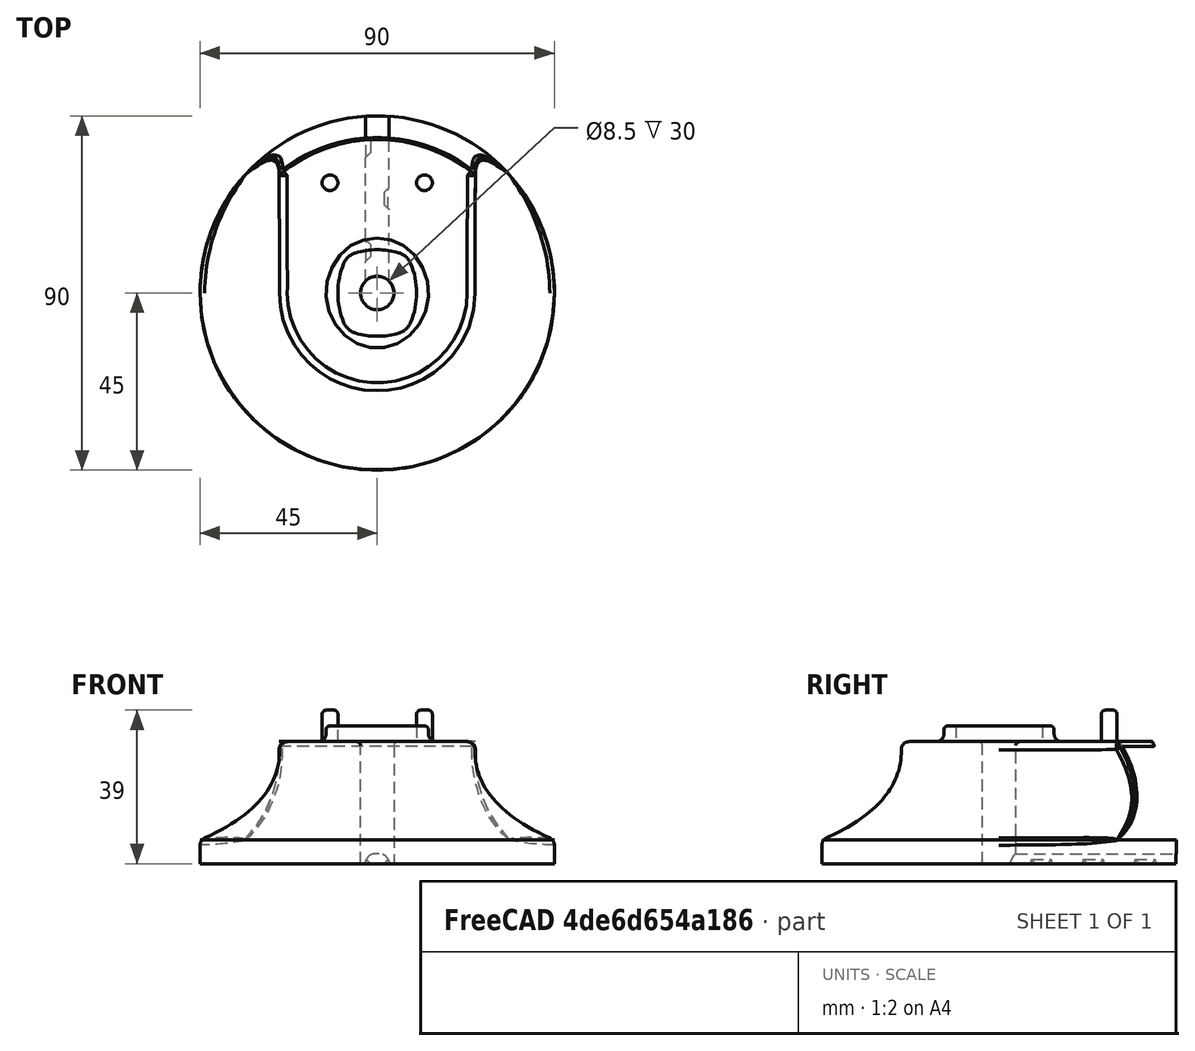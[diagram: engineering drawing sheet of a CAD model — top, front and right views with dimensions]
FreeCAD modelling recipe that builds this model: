
FCSTD DOCUMENT  (FreeCAD 1.0R39109 (Git))
Label: Toothbrush charging base
License: Creative Commons Attribution 4.0
LicenseURL: https://creativecommons.org/licenses/by/4.0/
objects: Sketcher::SketchObject×10, PartDesign::Pad×4, PartDesign::Pocket×3, PartDesign::Fillet×2, PartDesign::AdditiveLoft×1, PartDesign::Body×1
note: 51 computed .brp shape members not serialized (recipe doc carries the construction recipe); baked Part::Feature solids carry a one-line shape summary decoded from their .brp

FEATURE [Sketcher::SketchObject] Sketch
  ArcFitTolerance = 1e-06
  AttachmentSupport = -> [XY_Plane]
  FullyConstrained = true
  MakeInternals = false
  MapMode = 5
  sketch-geometry (1):
    g0: Circle CenterX=0 CenterY=0 CenterZ=0 NormalX=0 NormalY=0 NormalZ=1 AngleXU=0 Radius=45
  constraints (2):
    c: Diameter(g0) = 90
    c: Coincident(g0,g-1)
FEATURE [PartDesign::Pad] Pad
  Direction = (0,0,1)
  Length = 6
  Length2 = 10
  Profile = -> Sketch
  ReferenceAxis = -> Sketch [N_Axis]
  Suppressed = false
  Type = 0
FEATURE [Sketcher::SketchObject] Sketch001
  ArcFitTolerance = 1e-06
  AttachmentOffset = pos=(0,0,25) rot=(0,0,1;0rad)
  AttachmentSupport = -> [Pad]
  ExternalGeometry = -> [Pad]
  FullyConstrained = true
  MakeInternals = false
  MapMode = 5
  Placement = pos=(0,0,31) rot=(0,0,1;0rad)
  sketch-geometry (4):
    g0: ArcOfCircle CenterX=0 CenterY=0 CenterZ=0 NormalX=0 NormalY=0 NormalZ=1 AngleXU=0 Radius=39 StartAngle=0.874962 EndAngle=2.26663
    g1: ArcOfCircle CenterX=0 CenterY=0 CenterZ=0 NormalX=0 NormalY=0 NormalZ=1 AngleXU=0 Radius=25 StartAngle=3.14159 EndAngle=6.28319
    g2: LineSegment StartX=-25 StartY=29.9333 StartZ=0 EndX=-25 EndY=0 EndZ=0
    g3: LineSegment StartX=25 StartY=29.9333 StartZ=0 EndX=25 EndY=0 EndZ=0
  constraints (11):
    c: Coincident(g0,g-1)
    c: Coincident(g1,g0)
    c: PointOnObject(g1,g-1)
    c: PointOnObject(g1,g-1)
    c: DistanceX(g1,g1) = 50
    c: Vertical(g0,g1)
    c: Distance(g0,g-3) = 6
    c: Coincident(g2,g0)
    c: Coincident(g2,g1)
    c: Coincident(g3,g0)
    c: Tangent(g3,g1) = 1.5708
FEATURE [Sketcher::SketchObject] Sketch002
  ArcFitTolerance = 1e-06
  AttachmentOffset = pos=(0,0,20) rot=(0,0,1;0rad)
  AttachmentSupport = -> [Pad]
  ExternalGeometry = -> [Pad,Sketch001]
  FullyConstrained = true
  MakeInternals = false
  MapMode = 5
  Placement = pos=(0,0,26) rot=(0,0,1;0rad)
  sketch-geometry (4):
    g0: ArcOfCircle CenterX=0 CenterY=0 CenterZ=0 NormalX=0 NormalY=0 NormalZ=1 AngleXU=0 Radius=25 StartAngle=3.14159 EndAngle=6.28319
    g1: ArcOfCircle CenterX=0 CenterY=0 CenterZ=0 NormalX=0 NormalY=0 NormalZ=1 AngleXU=0 Radius=41 StartAngle=0.915044 EndAngle=2.22655
    g2: LineSegment StartX=-25 StartY=32.4962 StartZ=0 EndX=-25 EndY=0 EndZ=0
    g3: LineSegment StartX=25 StartY=32.4962 StartZ=0 EndX=25 EndY=0 EndZ=0
  constraints (11):
    c: Coincident(g0,g-1)
    c: Coincident(g0,g-4)
    c: Coincident(g1,g0)
    c: Vertical(g1,g0)
    c: Vertical(g1,g0)
    c: Coincident(g2,g1)
    c: Coincident(g2,g0)
    c: Coincident(g3,g1)
    c: Coincident(g3,g0)
    c: Horizontal(g0,g0)
    c: Distance(g1,g-3) = 4
FEATURE [Sketcher::SketchObject] Sketch003
  ArcFitTolerance = 1e-06
  AttachmentSupport = -> [Pad]
  ExternalGeometry = -> [Pad,Sketch001]
  FullyConstrained = true
  MakeInternals = false
  MapMode = 5
  Placement = pos=(0,0,6) rot=(0,0,1;0rad)
  sketch-geometry (4):
    g0: ArcOfCircle CenterX=0 CenterY=0 CenterZ=0 NormalX=0 NormalY=0 NormalZ=1 AngleXU=0 Radius=45 StartAngle=3.14159 EndAngle=6.28319
    g1: ArcOfCircle CenterX=0 CenterY=0 CenterZ=0 NormalX=0 NormalY=0 NormalZ=1 AngleXU=0 Radius=45 StartAngle=2.41385 EndAngle=3.14159
    g2: ArcOfCircle CenterX=-9e-16 CenterY=1.2e-15 CenterZ=0 NormalX=0 NormalY=0 NormalZ=1 AngleXU=0 Radius=45 StartAngle=0 EndAngle=0.72774
    g3: ArcOfCircle CenterX=-9e-16 CenterY=1.2e-15 CenterZ=0 NormalX=0 NormalY=0 NormalZ=1 AngleXU=0 Radius=45 StartAngle=0.72774 EndAngle=2.41385
  constraints (13):
    c: Coincident(g0,g-1)
    c: Horizontal(g0,g0)
    c: PointOnObject(g0,g-1)
    c: Coincident(g1,g0)
    c: Coincident(g1,g0)
    c: PointOnObject(g1,g-3)
    c: Horizontal(g1,g2)
    c: Coincident(g3,g2)
    c: Coincident(g3,g1)
    c: Coincident(g3,g2)
    c: Horizontal(g1,g-4)
    c: Coincident(g2,g0)
    c: PointOnObject(g2,g-3)
FEATURE [PartDesign::AdditiveLoft] AdditiveLoft
  BaseFeature = -> Pad
  Closed = false
  Profile = -> Sketch003
  Ruled = false
  Sections = -> [Sketch002,Sketch001]
  Suppressed = false
FEATURE [Sketcher::SketchObject] Sketch004
  ArcFitTolerance = 1e-06
  AttachmentSupport = -> [AdditiveLoft]
  FullyConstrained = true
  MakeInternals = false
  MapMode = 5
  Placement = pos=(0,0,31) rot=(0,0,1;0rad)
  sketch-geometry (18):
    g0: LineSegment [constr] StartX=-10 StartY=-11 StartZ=0 EndX=10 EndY=-11 EndZ=0
    g1: LineSegment [constr] StartX=10 StartY=-11 StartZ=0 EndX=10 EndY=11 EndZ=0
    g2: LineSegment [constr] StartX=10 StartY=11 StartZ=0 EndX=-10 EndY=11 EndZ=0
    g3: LineSegment [constr] StartX=-10 StartY=11 StartZ=0 EndX=-10 EndY=-11 EndZ=0
    g4: GeomPoint [constr] X=0 Y=0 Z=0
    g5: ArcOfCircle CenterX=0 CenterY=-8.28259 CenterZ=0 NormalX=0 NormalY=0 NormalZ=1 AngleXU=0 Radius=19.2826 StartAngle=1.28155 EndAngle=1.86004
    g6: ArcOfCircle CenterX=0 CenterY=8.28259 CenterZ=0 NormalX=0 NormalY=0 NormalZ=1 AngleXU=0 Radius=19.2826 StartAngle=4.42314 EndAngle=5.00164
    g7: ArcOfCircle CenterX=-9.5 CenterY=0 CenterZ=0 NormalX=0 NormalY=0 NormalZ=1 AngleXU=0 Radius=19.5 StartAngle=5.88839 EndAngle=6.67798
    g8: ArcOfCircle CenterX=9.5 CenterY=0 CenterZ=0 NormalX=0 NormalY=0 NormalZ=1 AngleXU=0 Radius=19.5 StartAngle=2.7468 EndAngle=3.53638
    g9: ArcOfCircle CenterX=-4.15846 CenterY=5.69103 CenterZ=0 NormalX=0 NormalY=0 NormalZ=1 AngleXU=0 Radius=4.70333 StartAngle=1.86004 EndAngle=2.7468
    g10: ArcOfCircle CenterX=4.15846 CenterY=5.69103 CenterZ=0 NormalX=0 NormalY=0 NormalZ=1 AngleXU=0 Radius=4.70333 StartAngle=0.394791 EndAngle=1.28155
    g11: ArcOfCircle CenterX=4.15846 CenterY=-5.69103 CenterZ=0 NormalX=0 NormalY=0 NormalZ=1 AngleXU=0 Radius=4.70333 StartAngle=5.00164 EndAngle=5.88839
    g12: ArcOfCircle CenterX=-4.15846 CenterY=-5.69103 CenterZ=0 NormalX=0 NormalY=0 NormalZ=1 AngleXU=0 Radius=4.70333 StartAngle=3.53638 EndAngle=4.42314
    g13: Ellipse CenterX=0 CenterY=0 CenterZ=0 NormalX=0 NormalY=0 NormalZ=1 MajorRadius=14 MinorRadius=13 AngleXU=1.5708
    g14: LineSegment [constr] StartX=0 StartY=14 StartZ=0 EndX=0 EndY=-14 EndZ=0
    g15: LineSegment [constr] StartX=-13 StartY=0 StartZ=0 EndX=13 EndY=0 EndZ=0
    g16: GeomPoint [constr] X=0 Y=5.19615 Z=0
    g17: GeomPoint [constr] X=0 Y=-5.19615 Z=0
  constraints (38):
    c: Coincident(g0,g1)
    c: Coincident(g1,g2)
    c: Coincident(g2,g3)
    c: Coincident(g3,g0)
    c: Horizontal(g0)
    c: Horizontal(g2)
    c: Vertical(g1)
    c: Vertical(g3)
    c: Symmetric(g2,g0,g4)
    c: Distance(g1,g3) = 20
    c: Distance(g0,g2) = 22
    c: Coincident(g4,g-1)
    c: PointOnObject(g5,g-2)
    c: Horizontal(g5,g5)
    c: Tangent(g5,g2)
    c: Symmetric(g6,g5,g4)
    c: Symmetric(g6,g5,g4)
    c: Horizontal(g6,g6)
    c: PointOnObject(g7,g-1)
    c: Tangent(g7,g1)
    c: Symmetric(g7,g8,g4)
    c: DistanceX(g5,g5) = 11
    c: DistanceY(g7,g7) = 15
    c: Tangent(g9,g5) = -1.5708
    c: Tangent(g9,g8) = -1.5708
    c: Tangent(g10,g5) = -1.5708
    c: Tangent(g10,g7) = -1.5708
    c: Tangent(g11,g7) = -1.5708
    c: Tangent(g11,g6) = -1.5708
    c: Tangent(g12,g6) = -1.5708
    c: Tangent(g12,g8) = -1.5708
    c: Equal(g9,g10)
    c: InternalAlignment(g14-g17 -> g13) x4
    c: Distance(g13,g15) = 13
    c: Angle(g15) = 0
    c: Distance(g13,g14) = 14
    c: Coincident(g13,g4)
    c: DistanceX(g7,g8) = 19
FEATURE [PartDesign::Pad] Pad001
  BaseFeature = -> AdditiveLoft
  Direction = (0,0,1)
  Length = 4
  Length2 = 10
  Profile = -> Sketch004
  ReferenceAxis = -> Sketch004 [N_Axis]
  Suppressed = false
  Type = 0
FEATURE [Sketcher::SketchObject] Sketch005
  ArcFitTolerance = 1e-06
  AttachmentSupport = -> [Pad001]
  FullyConstrained = true
  MakeInternals = false
  MapMode = 5
  Placement = pos=(0,0,31) rot=(0,0,1;0rad)
  sketch-geometry (2):
    g0: Circle CenterX=-12 CenterY=28 CenterZ=0 NormalX=0 NormalY=0 NormalZ=1 AngleXU=0 Radius=2
    g1: Circle CenterX=12 CenterY=28 CenterZ=0 NormalX=0 NormalY=0 NormalZ=1 AngleXU=0 Radius=2
  constraints (5):
    c: Diameter(g0) = 4
    c: Equal(g0,g1)
    c: Symmetric(g0,g1,g-2)
    c: DistanceY(g-1,g1) = 28
    c: DistanceX(g0,g1) = 24
FEATURE [PartDesign::Pad] Pad002
  BaseFeature = -> Pad001
  Direction = (0,0,1)
  Length = 8
  Length2 = 10
  Profile = -> Sketch005
  ReferenceAxis = -> Sketch005 [N_Axis]
  Suppressed = false
  Type = 0
FEATURE [Sketcher::SketchObject] Sketch006
  ArcFitTolerance = 1e-06
  AttachmentSupport = -> [Pad002]
  FullyConstrained = true
  MakeInternals = false
  MapMode = 5
  Placement = pos=(0,0,31) rot=(0,0,1;0rad)
  sketch-geometry (1):
    g0: Circle CenterX=0 CenterY=0 CenterZ=0 NormalX=0 NormalY=0 NormalZ=1 AngleXU=0 Radius=4.25
  constraints (2):
    c: Diameter(g0) = 8.5
    c: Coincident(g0,g-1)
FEATURE [PartDesign::Pocket] Pocket
  BaseFeature = -> Pad002
  Direction = (0,0,-1)
  Length = 5
  Length2 = 5
  Profile = -> Sketch006
  ReferenceAxis = -> Sketch006 [N_Axis]
  Suppressed = false
  Type = 1
FEATURE [Sketcher::SketchObject] Sketch007
  ArcFitTolerance = 1e-06
  AttachmentSupport = -> [XZ_Plane]
  FullyConstrained = true
  MakeInternals = false
  MapMode = 5
  Placement = pos=(0,0,0) rot=(1,0,0;1.5708rad)
  sketch-geometry (4):
    g0: ArcOfCircle CenterX=-0.5 CenterY=0 CenterZ=0 NormalX=0 NormalY=0 NormalZ=1 AngleXU=0 Radius=2.5 StartAngle=1.5708 EndAngle=3.14159
    g1: ArcOfCircle CenterX=0.5 CenterY=0 CenterZ=0 NormalX=0 NormalY=0 NormalZ=1 AngleXU=0 Radius=2.5 StartAngle=0 EndAngle=1.5708
    g2: LineSegment StartX=-0.5 StartY=2.5 StartZ=0 EndX=0.5 EndY=2.5 EndZ=0
    g3: LineSegment StartX=-3 StartY=0 StartZ=0 EndX=3 EndY=0 EndZ=0
  constraints (13):
    c: PointOnObject(g0,g-1)
    c: Vertical(g0,g0)
    c: Radius(g0) = 2.5
    c: Vertical(g1,g1)
    c: Horizontal(g0,g1)
    c: Coincident(g2,g0)
    c: Coincident(g2,g1)
    c: DistanceX(g0,g1) = 6
    c: PointOnObject(g0,g-1)
    c: PointOnObject(g1,g-1)
    c: Symmetric(g0,g1,g-1)
    c: Coincident(g3,g0)
    c: Coincident(g3,g1)
FEATURE [PartDesign::Pocket] Pocket001
  BaseFeature = -> Pocket
  Direction = (0,1,-2e-16)
  Length = 5
  Length2 = 5
  Profile = -> Sketch007
  ReferenceAxis = -> Sketch007 [N_Axis]
  Suppressed = false
  Type = 1
FEATURE [Sketcher::SketchObject] Sketch008
  ArcFitTolerance = 1e-06
  AttachmentSupport = -> [Pocket001]
  ExternalGeometry = -> [Pocket001]
  FullyConstrained = true
  MakeInternals = false
  MapMode = 5
  Placement = pos=(0,0,0) rot=(1,0,0;3.14159rad)
  sketch-geometry (16):
    g0: LineSegment StartX=-3 StartY=-39.8999 StartZ=0 EndX=-1.75 EndY=-38.6499 EndZ=0
    g1: LineSegment StartX=-1.75 StartY=-38.6499 StartZ=0 EndX=-1.75 EndY=-35.6499 EndZ=0
    g2: LineSegment StartX=-1.75 StartY=-35.6499 StartZ=0 EndX=-3 EndY=-34.3999 EndZ=0
    g3: LineSegment StartX=3 StartY=-26.7051 StartZ=0 EndX=1.75 EndY=-25.4551 EndZ=0
    g4: LineSegment StartX=1.75 StartY=-25.4551 StartZ=0 EndX=1.75 EndY=-22.4551 EndZ=0
    g5: LineSegment StartX=1.75 StartY=-22.4551 StartZ=0 EndX=3 EndY=-21.2051 EndZ=0
    g6: LineSegment StartX=3 StartY=-21.2051 StartZ=0 EndX=3 EndY=-26.7051 EndZ=0
    g7: LineSegment StartX=-3 StartY=-34.3999 StartZ=0 EndX=-3 EndY=-39.8999 EndZ=0
    g8: LineSegment StartX=-3 StartY=-13.5104 StartZ=0 EndX=-1.75 EndY=-12.2604 EndZ=0
    g9: LineSegment StartX=-1.75 StartY=-12.2604 StartZ=0 EndX=-1.75 EndY=-9.2604 EndZ=0
    g10: LineSegment StartX=-1.75 StartY=-9.2604 StartZ=0 EndX=-3 EndY=-8.0104 EndZ=0
    g11: LineSegment StartX=-3 StartY=-8.0104 StartZ=0 EndX=-3 EndY=-13.5104 EndZ=0
    g12: GeomPoint [constr] X=-3 Y=-10.7604 Z=0
    g13: GeomPoint [constr] X=3 Y=-23.9551 Z=0
    g14: GeomPoint [constr] X=-3 Y=-37.1499 Z=0
    g15: GeomPoint [constr] X=-3 Y=-23.9551 Z=0
  constraints (39):
    c: PointOnObject(g0,g-3)
    c: Coincident(g1,g0)
    c: Vertical(g1)
    c: Coincident(g2,g1)
    c: PointOnObject(g2,g-3)
    c: Angle(g-3,g0) = 2.35619
    c: Angle(g2,g-3) = 2.35619
    c: DistanceX(g0,g0) = 1.25
    c: DistanceY(g0,g1) = 3
    c: DistanceY(g-3,g0) = 5
    c: Coincident(g3,g4)
    c: Vertical(g4)
    c: Coincident(g4,g5)
    c: PointOnObject(g5,g-4)
    c: Coincident(g5,g6)
    c: Coincident(g6,g3)
    c: Coincident(g2,g7)
    c: Coincident(g7,g0)
    c: PointOnObject(g8,g-3)
    c: Coincident(g8,g9)
    c: Vertical(g9)
    c: Coincident(g9,g10)
    c: Coincident(g10,g11)
    c: Coincident(g11,g8)
    c: Equal(g1,g4)
    c: Angle(g5,g6) = 0.785398
    c: Angle(g6,g3) = 0.785398
    c: DistanceX(g3,g3) = 1.25
    c: Angle(g11,g10) = 0.785398
    c: Angle(g8,g11) = 0.785398
    c: Equal(g9,g4)
    c: Vertical(g1,g8)
    c: PointOnObject(g3,g-4)
    c: Symmetric(g11,g11,g12)
    c: Symmetric(g6,g6,g13)
    c: Symmetric(g7,g7,g14)
    c: Symmetric(g-3,g-3,g15)
    c: Symmetric(g12,g14,g15)
    c: Horizontal(g15,g13)
FEATURE [PartDesign::Pad] Pad003
  BaseFeature = -> Pocket001
  Direction = (0,0,-1)
  Length = 10
  Length2 = 10
  Profile = -> Sketch008
  ReferenceAxis = -> Sketch008 [N_Axis]
  Reversed = true
  Suppressed = false
  Type = 3
  UpToFace = -> Pocket001 [Face8]
FEATURE [Sketcher::SketchObject] Sketch009
  ArcFitTolerance = 1e-06
  AttachmentSupport = -> [XZ_Plane]
  ExternalGeometry = -> [Pad003]
  FullyConstrained = true
  MakeInternals = false
  MapMode = 5
  Placement = pos=(0,0,0) rot=(1,0,0;1.5708rad)
  sketch-geometry (6):
    g0: LineSegment StartX=1.75 StartY=5.7e-15 StartZ=0 EndX=2.77859 EndY=1.02859 EndZ=0
    g1: LineSegment StartX=-1.75 StartY=8.6e-15 StartZ=0 EndX=-2.77859 EndY=1.02859 EndZ=0
    g2: LineSegment StartX=0.5 StartY=2.5 StartZ=0 EndX=-0.5 EndY=2.5 EndZ=0
    g3: ArcOfCircle CenterX=0.5 CenterY=0 CenterZ=0 NormalX=0 NormalY=0 NormalZ=1 AngleXU=0 Radius=2.5 StartAngle=0.424031 EndAngle=1.5708
    g4: ArcOfCircle CenterX=-0.5 CenterY=0 CenterZ=0 NormalX=0 NormalY=0 NormalZ=1 AngleXU=0 Radius=2.5 StartAngle=1.5708 EndAngle=2.71756
    g5: LineSegment StartX=1.75 StartY=5.7e-15 StartZ=0 EndX=-1.75 EndY=8.6e-15 EndZ=0
  constraints (16):
    c: Coincident(g0,g-3)
    c: PointOnObject(g0,g-6)
    c: Angle(g-3,g0) = 0.785398
    c: Coincident(g1,g-4)
    c: PointOnObject(g1,g-5)
    c: Angle(g1,g-4) = 0.785398
    c: Coincident(g2,g-6)
    c: Coincident(g2,g-5)
    c: PointOnObject(g4,g-1)
    c: Coincident(g4,g1)
    c: Coincident(g4,g2)
    c: Coincident(g3,g0)
    c: Coincident(g3,g2)
    c: PointOnObject(g3,g-1)
    c: Coincident(g5,g0)
    c: Coincident(g5,g1)
FEATURE [PartDesign::Pocket] Pocket002
  BaseFeature = -> Pad003
  Direction = (0,1,-2e-16)
  Length = 5
  Length2 = 5
  Profile = -> Sketch009
  ReferenceAxis = -> Sketch009 [N_Axis]
  Refine = true
  Suppressed = false
  Type = 1
FEATURE [PartDesign::Fillet] Fillet
  Base = -> Pocket002 [Edge28,Edge15,Edge18,Edge20,Edge19,Edge10]
  BaseFeature = -> Pocket002
  Radius = 2
  SupportTransform = false
  Suppressed = false
  UseAllEdges = false
FEATURE [PartDesign::Fillet] Fillet001
  Base = -> Fillet [Edge120,Edge118,Edge121,Edge67]
  BaseFeature = -> Fillet
  Radius = 1
  SupportTransform = false
  Suppressed = false
  UseAllEdges = false
FEATURE [PartDesign::Body] Body
  AllowCompound = false
  Group = -> [Sketch,Pad,Sketch001,Sketch002,Sketch003,AdditiveLoft,Sketch004,Pad001,Sketch005,Pad002,Sketch006,Pocket,Sketch007,Pocket001,Sketch008,Pad003,Sketch009,Pocket002,Fillet,Fillet001]
  Origin = -> Origin
  Tip = -> Fillet001
